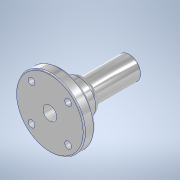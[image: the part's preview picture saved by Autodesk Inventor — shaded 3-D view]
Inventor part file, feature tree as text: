
AUTODESK INVENTOR PART (.ipt)
format: ipt  version: 2020.3 (Build 243373000, 373)  size: 192,512 bytes
history: native  units: mm
features: fillet x5, sketch x4, extrude x3, other x1, hole x1
ambient origin geometry x8: Origin, YZ Plane, XZ Plane, XY Plane, X Axis, Y Axis, Z Axis, Center Point
bodies: Body1 (feature_tree)
feature tree (14):
  other  "ソリッド1"
  extrude  "押し出し1"  Depth=15.0mm
  extrude  "押し出し2"  Depth=6.0mm
  hole  "穴1"  [1 undecoded]
  fillet  "フィレット1"  Radius=6.0mm
  fillet  "フィレット3"  Radius=30.0mm
  extrude  "押し出し3"  Depth=5.0mm TaperAngle=0.0deg
  fillet  "フィレット4"  Radius=8.0mm
  fillet  "フィレット5"  Radius=8.0mm
  fillet  "フィレット6"  Radius=16.0mm
  sketch  "スケッチ1"
  sketch  "スケッチ2"
  sketch  "スケッチ3"
  sketch  "スケッチ4"
note: 1 required parameter value undecoded (feature->parameter linkage not recoverable at this tier; creation-order binding heuristic only, values carry confidence <= 0.55)
